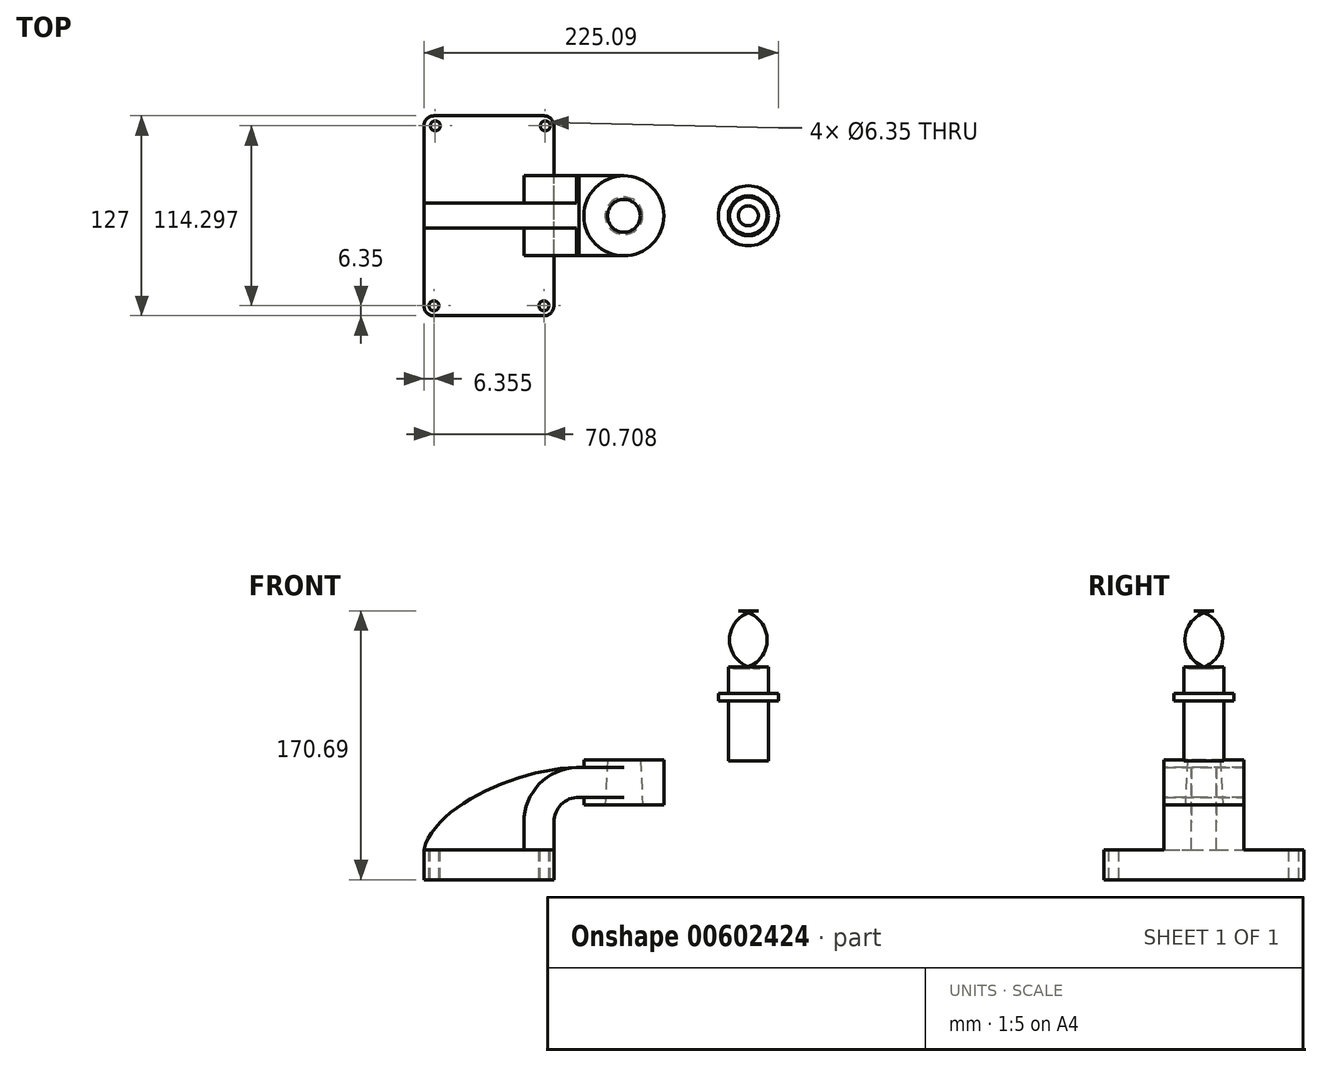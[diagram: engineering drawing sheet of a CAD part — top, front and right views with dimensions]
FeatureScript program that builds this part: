
annotation { "Feature Type Name" : "Feature", "Feature Type Description" : "" }
export const myFeature = defineFeature(function(context is Context, id is Id, definition is map)
    precondition{}
    {
        {
            var Q0;
            Q0=qCreatedBy(makeId("Front.planeOp"),FACE);
            var sketch = newSketch(context, id + "F0", { "sketchPlane" : qUnion([Q0])});
            skLineSegment(sketch, "E0.bottom", {"start": v(41.28, -8.48) * mm, "end": v(-41.28, -8.48) * mm});
            skLineSegment(sketch, "E0.top", {"start": v(41.28, 10.57) * mm, "end": v(-41.28, 10.57) * mm});
            skLineSegment(sketch, "E0.left", {"start": v(41.28, -8.48) * mm, "end": v(41.28, 10.57) * mm});
            skLineSegment(sketch, "E0.right", {"start": v(-41.28, -8.48) * mm, "end": v(-41.28, 10.57) * mm});
            skPoint(sketch, "E0.middle", {"position": v(0, 1.04) * mm});
            skLineSegment(sketch, "E1.bottom", {"start": v(60.33, 39.14) * mm, "end": v(111.12, 39.14) * mm});
            skLineSegment(sketch, "E1.top", {"start": v(60.32, 67.72) * mm, "end": v(111.12, 67.72) * mm});
            skLineSegment(sketch, "E1.left", {"start": v(60.33, 39.14) * mm, "end": v(60.32, 67.72) * mm});
            skLineSegment(sketch, "E1.right", {"start": v(111.12, 39.14) * mm, "end": v(111.12, 67.72) * mm});
            skPoint(sketch, "E1.middle", {"position": v(85.73, 53.43) * mm});
            skLineSegment(sketch, "E2", {"start": v(41.27, 10.57) * mm, "end": v(41.27, 28.04) * mm});
            skArc(sketch, "E3", {"start": v(41.27, 28.04) * mm, "mid": v(45.92, 39.27) * mm, "end": v(57.15, 43.92) * mm});
            skLineSegment(sketch, "E4", {"start": v(57.15, 43.92) * mm, "end": v(85.73, 43.92) * mm});
            skLineSegment(sketch, "E5.0", {"start": v(57.15, 62.97) * mm, "end": v(85.72, 62.97) * mm});
            skArc(sketch, "E5.1", {"start": v(22.23, 28.04) * mm, "mid": v(32.45, 52.74) * mm, "end": v(57.15, 62.97) * mm});
            skLineSegment(sketch, "E5.2", {"start": v(22.23, 10.57) * mm, "end": v(22.23, 28.04) * mm});
            skLineSegment(sketch, "E6", {"start": v(85.72, 39.14) * mm, "end": v(85.72, 67.72) * mm});
            skFitSpline(sketch, "E7", {"points": [v(-41.28, 10.57) * mm, v(57.15, 62.97) * mm], "startDerivative": vector(19.67, 84.26) * mm, "endDerivative": vector(113.6, 1.52) * mm});
            skSolve(sketch);
        }
        {
            var Q0;
            Q0=makeQuery(id+"F0.imprint","IMPRINT",FACE,{"disambiguationData":[TD([[makeQuery(id+"F0.imprint","IMPRINT",EDGE,{"derivedFrom":sQuery(id+"F0.wireOp",EDGE,"E0.bottom")}),-1.0]])]});
            extrude(context, id + "F1", {"entities" : qUnion([Q0]), "endBound" : BoundingType.SYMMETRIC, "depth" : 127 * mm});
        }
        {
            var Q0;
            {var subQ1=sQuery(id+"F0.wireOp",EDGE,"E2");Q0=makeQuery(id+"F0.imprint","IMPRINT",FACE,{"disambiguationData":[TD([[makeQuery(id+"F0.imprint","IMPRINT",EDGE,{"derivedFrom":subQ1}),1.0]])]});}
            var Q1;
            {var subQ0=sQuery(id+"F0.wireOp",EDGE,"E4");var subQ1=sQuery(id+"F0.wireOp",EDGE,"E1.left");var subQ2=makeQuery(id+"F0.imprint","INTERSECT",VERTEX,{"derivedFrom":[subQ1,subQ0]});Q1=makeQuery(id+"F0.imprint","IMPRINT",FACE,{"disambiguationData":[TD([[makeQuery(id+"F0.imprint","IMPRINT",EDGE,{"disambiguationData":[TD([[subQ2,-1.0]])],"derivedFrom":subQ1}),-1.0]])]});}
            extrude(context, id + "F2", {"entities" : qUnion([Q0, Q1]), "operationType" : NewBodyOperationType.ADD, "endBound" : BoundingType.SYMMETRIC, "depth" : 50.8 * mm});
        }
        {
            var Q0;
            {var subQ3=sQuery(id+"F0.wireOp",EDGE,"E5.2");Q0=makeQuery(id+"F0.imprint","IMPRINT",FACE,{"disambiguationData":[TD([[makeQuery(id+"F0.imprint","IMPRINT",EDGE,{"derivedFrom":subQ3}),1.0]])]});}
            extrude(context, id + "F3", {"entities" : qUnion([Q0]), "operationType" : NewBodyOperationType.ADD, "endBound" : BoundingType.SYMMETRIC, "depth" : 15.88 * mm});
        }
        {
            var Q0;
            {var subQ4=sQuery(id+"F0.wireOp",EDGE,"E1.right");Q0=makeQuery(id+"F0.imprint","IMPRINT",FACE,{"disambiguationData":[TD([[makeQuery(id+"F0.imprint","IMPRINT",EDGE,{"derivedFrom":subQ4}),1.0]])]});}
            var Q1;
            Q1=sQuery(id+"F0.wireOp",EDGE,"E6");
            revolve(context, id + "F4", {"operationType" : NewBodyOperationType.ADD, "entities" : qUnion([Q0]), "axis" : qUnion([Q1]), "revolveType" : RevolveType.FULL});
        }
        {
            var Q0;
            Q0=makeQuery(id+"F1.opExtrude","CAP_EDGE",EDGE,{"disambiguationData":[OSD([sQuery(id+"F0.wireOp",EDGE,"E0.right")])],"isStart":false});
            var Q1;
            Q1=makeQuery(id+"F1.opExtrude","CAP_EDGE",EDGE,{"disambiguationData":[OSD([sQuery(id+"F0.wireOp",EDGE,"E0.left")])],"isStart":false});
            var Q2;
            Q2=makeQuery(id+"F1.opExtrude","CAP_EDGE",EDGE,{"disambiguationData":[OSD([sQuery(id+"F0.wireOp",EDGE,"E0.left")])],"isStart":true});
            var Q3;
            Q3=makeQuery(id+"F1.opExtrude","CAP_EDGE",EDGE,{"disambiguationData":[OSD([sQuery(id+"F0.wireOp",EDGE,"E0.right")])],"isStart":true});
            fillet(context, id + "F5", {"entities" : qUnion([Q0, Q1, Q2, Q3]), "radius" : 6.35 * mm, "tangentPropagation" : true, "allowEdgeOverflow" : false});
        }
        {
            var Q0;
            Q0=makeQuery(id+"F4.opRevolve","SWEPT_FACE",FACE,{"disambiguationData":[OSD([sQuery(id+"F0.wireOp",EDGE,"E1.top")])]});
            var sketch = newSketch(context, id + "F6", { "sketchPlane" : qUnion([Q0])});
            skCircle(sketch, "E8", {"center": v(85.72, 0) * mm, "radius": 10.43 * mm});
            skSolve(sketch);
        }
        {
            var Q0;
            Q0=qSketchRegion(id+"F6",true);
            extrude(context, id + "F7", {"entities" : qUnion([Q0]), "operationType" : NewBodyOperationType.REMOVE, "endBound" : BoundingType.THROUGH_ALL, "oppositeDirection" : true, "depth" : 25.4 * mm, "hasDraft" : true, "draftAngle" : 3 * degree});
        }
        {
            var Q0;
            {var subQ4=sQuery(id+"F0.wireOp",EDGE,"E0.top");var subQ5=sQuery(id+"F0.wireOp",EDGE,"E0.right");var subQ6=sQuery(id+"F0.wireOp",EDGE,"E0.left");Q0=makeQuery(id+"F3.boolean.opBoolean","SPLIT",FACE,{"disambiguationData":[TD([makeQuery(id+"F1.opExtrude","CAP_FACE",FACE,{"disambiguationData":[OSD([sQuery(id+"F0.wireOp",EDGE,"E0.bottom"),subQ4,subQ6,subQ5])],"isStart":false})])],"derivedFrom":makeQuery(id+"F1.opExtrude","SWEPT_FACE",FACE,{"disambiguationData":[OSD([subQ4])]})});}
            var sketch = newSketch(context, id + "F8", { "sketchPlane" : qUnion([Q0])});
            skCircle(sketch, "E9", {"center": v(-34.93, -57.15) * mm, "radius": 3.17 * mm});
            skCircle(sketch, "E10.0.1.0", {"center": v(-34.07, 57.15) * mm, "radius": 3.17 * mm});
            skCircle(sketch, "E10.1.0.0", {"center": v(34.92, -57.15) * mm, "radius": 3.17 * mm});
            skCircle(sketch, "E10.1.1.0", {"center": v(35.78, 57.15) * mm, "radius": 3.17 * mm});
            skLineSegment(sketch, "E10.direction1", {"start": v(-34.93, -57.15) * mm, "end": v(34.92, -57.15) * mm, "construction": true});
            skLineSegment(sketch, "E10.direction2", {"start": v(-34.92, -57.15) * mm, "end": v(-34.07, 57.15) * mm, "construction": true});
            skSolve(sketch);
        }
        {
            var Q0;
            Q0=sQuery(id+"F8.wireOp",VERTEX,"E10.1.0.0.center");
            var Q1;
            Q1=sQuery(id+"F8.wireOp",VERTEX,"E9.center");
            var Q2;
            Q2=sQuery(id+"F8.wireOp",VERTEX,"E10.1.1.0.center");
            var Q3;
            Q3=sQuery(id+"F8.wireOp",VERTEX,"E10.0.1.0.center");
            var Q4;
            Q4=makeQuery(id+"F1.opExtrude","SWEPT_BODY",BODY,{"disambiguationData":[OSD([sQuery(id+"F0.wireOp",EDGE,"E0.bottom"),sQuery(id+"F0.wireOp",EDGE,"E0.top"),sQuery(id+"F0.wireOp",EDGE,"E0.left"),sQuery(id+"F0.wireOp",EDGE,"E0.right")])]});
            hole(context, id + "F9", {"style" : HoleStyle.SIMPLE, "endStyle" : HoleEndStyle.THROUGH, "holeDiameter" : 6.35 * mm, "tappedDepth" : 12.7 * mm, "tapClearance" : 3, "locations" : qUnion([Q0, Q1, Q2, Q3]), "scope" : qUnion([Q4]), "majorDiameter" : 6.35 * mm});
        }
        {
            var Q0;
            Q0=qCreatedBy(makeId("Front.planeOp"),FACE);
            var sketch = newSketch(context, id + "F10", { "sketchPlane" : qUnion([Q0])});
            skLineSegment(sketch, "E11", {"start": v(164.76, 66.96) * mm, "end": v(177.46, 66.96) * mm});
            skLineSegment(sketch, "E12", {"start": v(177.46, 66.96) * mm, "end": v(177.46, 105.06) * mm});
            skLineSegment(sketch, "E13", {"start": v(177.46, 105.06) * mm, "end": v(183.8, 105.06) * mm});
            skLineSegment(sketch, "E14", {"start": v(183.8, 105.06) * mm, "end": v(183.8, 109.82) * mm});
            skLineSegment(sketch, "E15", {"start": v(183.8, 109.82) * mm, "end": v(177.46, 109.82) * mm});
            skLineSegment(sketch, "E16", {"start": v(164.76, 162.21) * mm, "end": v(171.1, 162.21) * mm});
            skLineSegment(sketch, "E17", {"start": v(164.76, 162.21) * mm, "end": v(164.76, 66.96) * mm});
            skLineSegment(sketch, "E18", {"start": v(171.1, 162.21) * mm, "end": v(171.1, 162.2) * mm});
            skArc(sketch, "E19", {"start": v(177.46, 126.71) * mm, "mid": v(189.13, 147.12) * mm, "end": v(171.1, 162.2) * mm});
            skLineSegment(sketch, "E20", {"start": v(177.46, 109.82) * mm, "end": v(177.46, 126.71) * mm});
            skSolve(sketch);
        }
        {
            var Q0;
            Q0=qSketchRegion(id+"F10",true);
            var Q1;
            Q1=sQuery(id+"F10.wireOp",EDGE,"E17");
            revolve(context, id + "F11", {"entities" : qUnion([Q0]), "axis" : qUnion([Q1]), "revolveType" : RevolveType.FULL});
        }
    });
